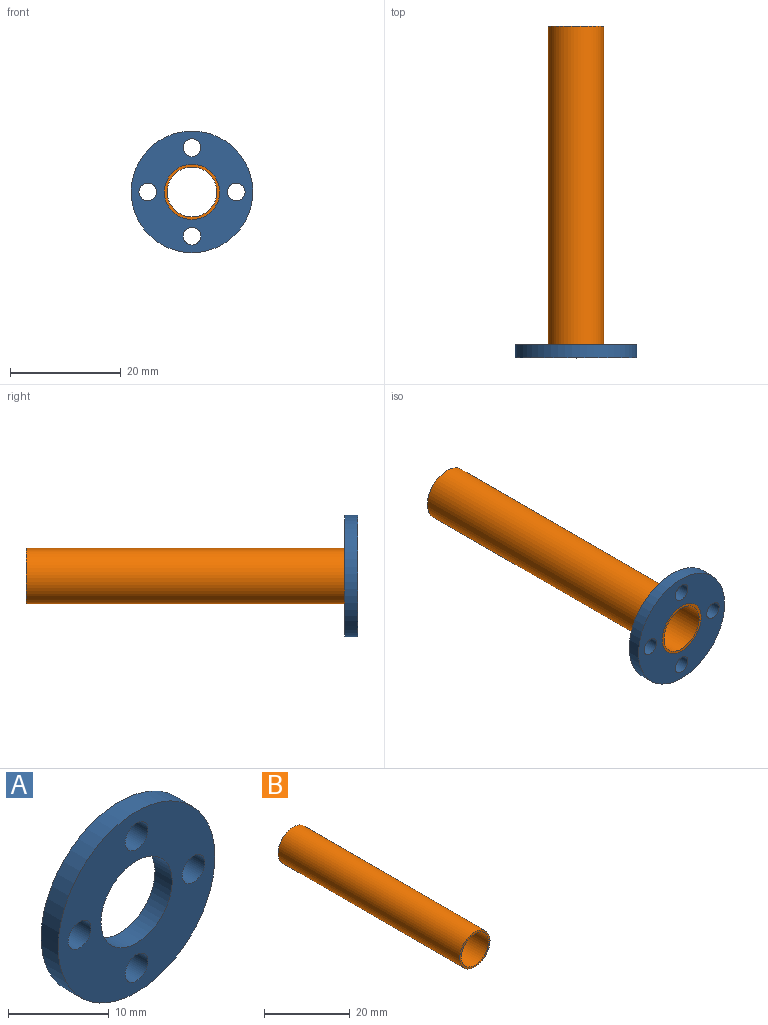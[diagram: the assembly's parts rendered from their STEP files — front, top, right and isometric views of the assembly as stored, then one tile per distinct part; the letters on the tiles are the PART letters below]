
ASSEMBLY  parts=2 mates=1
PART A: 8 faces, bbox 22x2.4x22 mm
  f0: cylinder r=5mm len=10mm, axis (0,1,0), area 75.4mm2, adj f6,f7
  f1: cylinder r=1.6mm len=3.2mm, axis (0,1,0), area 24.1mm2, adj f6,f7
  f2: cylinder r=1.6mm len=3.2mm, axis (0,1,0), area 24.1mm2, adj f6,f7
  f3: cylinder r=1.6mm len=3.2mm, axis (0,1,0), area 24.1mm2, adj f6,f7
  f4: cylinder r=1.6mm len=3.2mm, axis (0,1,0), area 24.1mm2, adj f6,f7
  f5: cylinder r=11mm len=22mm, axis (0,1,0), area 165.9mm2, adj f6,f7
  f6: plane 22x22mm, normal (0,-1,0), area 269.4mm2, adj f0,f1,f2,f3,f4,f5
  f7: plane 22x22mm, normal (0,1,0), area 269.4mm2, adj f0,f1,f2,f3,f4,f5
PART B: 4 faces, bbox 10x60x10 mm
  f0: cylinder r=4.5mm len=60mm, axis (0,1,0), area 1696.5mm2, adj f2,f3
  f1: cylinder r=5mm len=60mm, axis (0,1,0), area 1885mm2, adj f2,f3
  f2: plane 10x10mm, normal (0,-1,0), area 14.9mm2, adj f0,f1
  f3: plane 10x10mm, normal (0,1,0), area 14.9mm2, adj f0,f1
PLACE A t=(0,-28.8,0)mm
PLACE B at identity fixed
MATE fastened B.f0 <-> A.f5  axis (0,1,0) through (0,-30,0)mm
